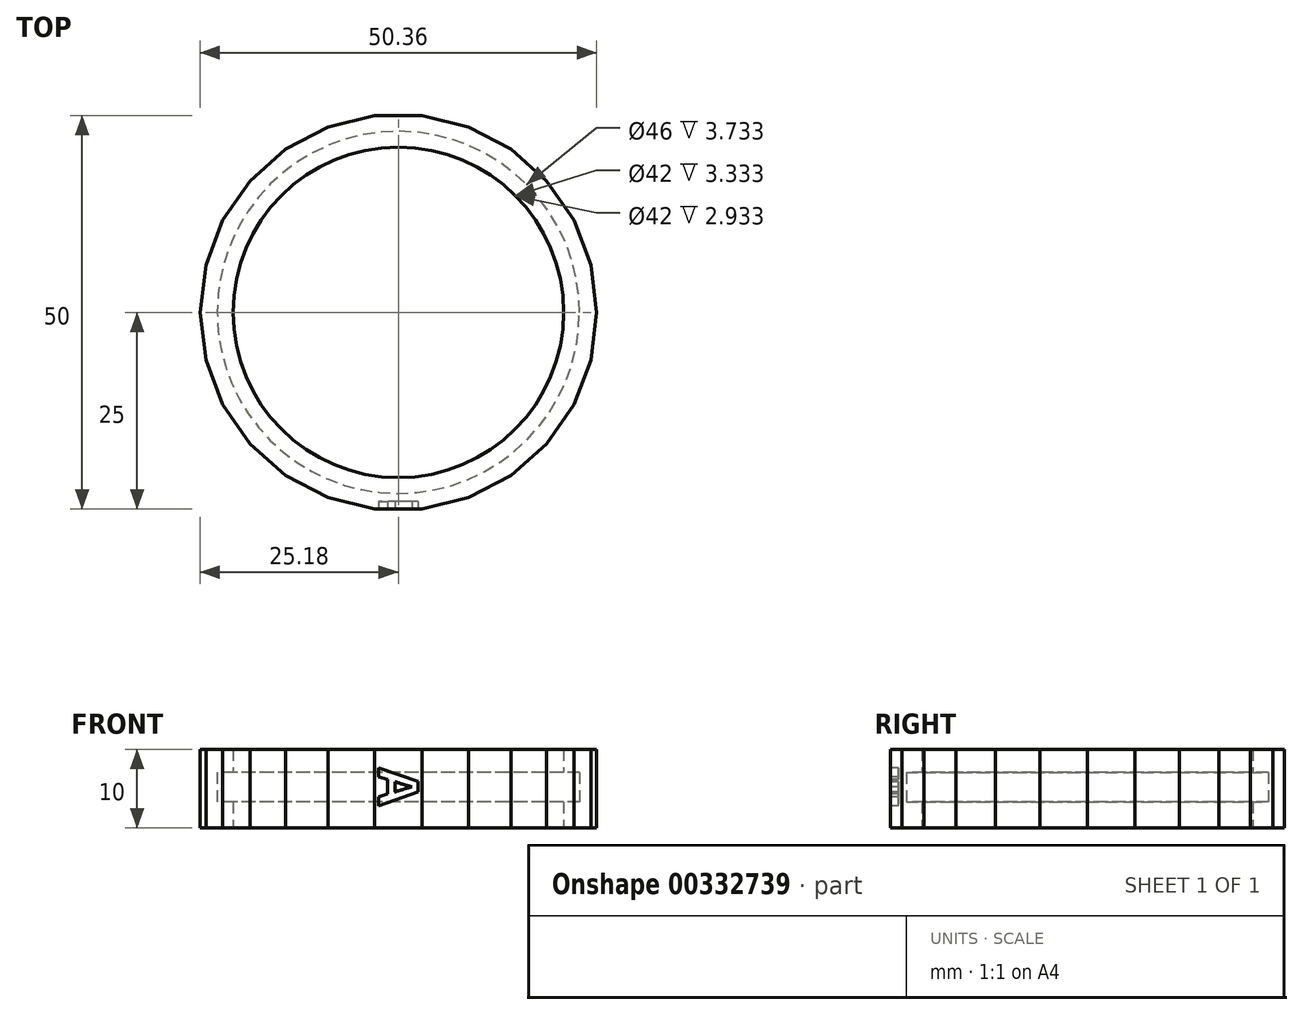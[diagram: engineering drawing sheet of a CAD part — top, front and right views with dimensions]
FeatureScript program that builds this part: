
annotation { "Feature Type Name" : "Feature", "Feature Type Description" : "" }
export const myFeature = defineFeature(function(context is Context, id is Id, definition is map)
    precondition{}
    {
        {
            assignVariable(context, id + "F0", {"name" : "thickness", "anyValue" : 2});
        }
        {
            var Q0;
            Q0=qCreatedBy(makeId("Top.planeOp"),FACE);
            var sketch = newSketch(context, id + "F1", { "sketchPlane" : qUnion([Q0])});
            skCircle(sketch, "E0", {"center": v(0, 0) * mm, "radius": 21 * mm});
            skCircle(sketch, "E1", {"center": v(0, 0) * mm, "radius": 23 * mm});
            skCircle(sketch, "E2.cCircle", {"center": v(0, 0) * mm, "radius": 25 * mm, "construction": true});
            skLineSegment(sketch, "E2.0", {"start": v(-3.04, 25) * mm, "end": v(3.04, 25) * mm});
            skLineSegment(sketch, "E2.1", {"start": v(3.04, 25) * mm, "end": v(8.93, 23.55) * mm});
            skLineSegment(sketch, "E2.2", {"start": v(8.93, 23.55) * mm, "end": v(14.3, 20.73) * mm});
            skLineSegment(sketch, "E2.3", {"start": v(14.3, 20.73) * mm, "end": v(18.85, 16.7) * mm});
            skLineSegment(sketch, "E2.4", {"start": v(18.85, 16.7) * mm, "end": v(22.3, 11.7) * mm});
            skLineSegment(sketch, "E2.5", {"start": v(22.3, 11.7) * mm, "end": v(24.45, 6.03) * mm});
            skLineSegment(sketch, "E2.6", {"start": v(24.45, 6.03) * mm, "end": v(25.18, 0) * mm});
            skLineSegment(sketch, "E2.7", {"start": v(25.18, 0) * mm, "end": v(24.45, -6.03) * mm});
            skLineSegment(sketch, "E2.8", {"start": v(24.45, -6.03) * mm, "end": v(22.3, -11.7) * mm});
            skLineSegment(sketch, "E2.9", {"start": v(22.3, -11.7) * mm, "end": v(18.85, -16.7) * mm});
            skLineSegment(sketch, "E2.10", {"start": v(18.85, -16.7) * mm, "end": v(14.3, -20.73) * mm});
            skLineSegment(sketch, "E2.11", {"start": v(14.3, -20.73) * mm, "end": v(8.93, -23.55) * mm});
            skLineSegment(sketch, "E2.12", {"start": v(8.93, -23.55) * mm, "end": v(3.04, -25) * mm});
            skLineSegment(sketch, "E2.13", {"start": v(3.04, -25) * mm, "end": v(-3.04, -25) * mm});
            skLineSegment(sketch, "E2.14", {"start": v(-3.04, -25) * mm, "end": v(-8.93, -23.55) * mm});
            skLineSegment(sketch, "E2.15", {"start": v(-8.93, -23.55) * mm, "end": v(-14.3, -20.73) * mm});
            skLineSegment(sketch, "E2.16", {"start": v(-14.3, -20.73) * mm, "end": v(-18.85, -16.7) * mm});
            skLineSegment(sketch, "E2.17", {"start": v(-18.85, -16.7) * mm, "end": v(-22.3, -11.7) * mm});
            skLineSegment(sketch, "E2.18", {"start": v(-22.3, -11.7) * mm, "end": v(-24.45, -6.03) * mm});
            skLineSegment(sketch, "E2.19", {"start": v(-24.45, -6.03) * mm, "end": v(-25.18, 0) * mm});
            skLineSegment(sketch, "E2.20", {"start": v(-25.18, 0) * mm, "end": v(-24.45, 6.03) * mm});
            skLineSegment(sketch, "E2.21", {"start": v(-24.45, 6.03) * mm, "end": v(-22.3, 11.7) * mm});
            skLineSegment(sketch, "E2.22", {"start": v(-22.3, 11.7) * mm, "end": v(-18.85, 16.7) * mm});
            skLineSegment(sketch, "E2.23", {"start": v(-18.85, 16.7) * mm, "end": v(-14.3, 20.73) * mm});
            skLineSegment(sketch, "E2.24", {"start": v(-14.3, 20.73) * mm, "end": v(-8.93, 23.55) * mm});
            skLineSegment(sketch, "E2.25", {"start": v(-8.93, 23.55) * mm, "end": v(-3.04, 25) * mm});
            skPoint(sketch, "E2.0.midPoint", {"position": v(0, 25) * mm});
            skSolve(sketch);
        }
        {
            var Q0;
            Q0=qCreatedBy(makeId("Front.planeOp"),FACE);
            var sketch = newSketch(context, id + "F2", { "sketchPlane" : qUnion([Q0])});
            skLineSegment(sketch, "E3", {"start": v(0, 10) * mm, "end": v(0, 0) * mm, "construction": true});
            skPoint(sketch, "E4", {"position": v(0, 10.4) * mm});
            skPoint(sketch, "E5", {"position": v(0, 6.67) * mm});
            skPoint(sketch, "E6", {"position": v(0, 3.33) * mm});
            skPoint(sketch, "E7", {"position": v(0, 3.73) * mm});
            skPoint(sketch, "E8", {"position": v(0, 7.07) * mm});
            skPoint(sketch, "E9", {"position": v(0, 5) * mm});
            skPoint(sketch, "E10", {"position": v(0, 5.4) * mm});
            skSolve(sketch);
        }
        {
            var Q0;
            Q0=makeQuery(id+"F1.imprint","IMPRINT",FACE,{"disambiguationData":[TD([[makeQuery(id+"F1.imprint","IMPRINT",EDGE,{"derivedFrom":sQuery(id+"F1.wireOp",EDGE,"E1")}),-1.0]])]});
            var Q1;
            Q1=sQuery(id+"F2.wireOp",VERTEX,"E3.start");
            extrude(context, id + "F3", {"entities" : qUnion([Q0]), "endBound" : BoundingType.UP_TO_VERTEX, "endBoundEntityVertex" : qUnion([Q1]), "depth" : 25 * mm});
        }
        {
            var Q0;
            Q0=makeQuery(id+"F1.imprint","IMPRINT",FACE,{"disambiguationData":[TD([[makeQuery(id+"F1.imprint","IMPRINT",EDGE,{"derivedFrom":sQuery(id+"F1.wireOp",EDGE,"E0")}),-1.0]])]});
            var Q1;
            Q1=sQuery(id+"F2.wireOp",VERTEX,"E6");
            var Q2;
            Q2=sQuery(id+"F2.wireOp",VERTEX,"E6");
            extrude(context, id + "F4", {"entities" : qUnion([Q0]), "operationType" : NewBodyOperationType.ADD, "endBound" : BoundingType.UP_TO_VERTEX, "endBoundEntityVertex" : qUnion([Q1]), "depth" : 25 * mm});
        }
        {
            var Q0;
            Q0=makeQuery(id+"F1.imprint","IMPRINT",FACE,{"disambiguationData":[TD([[makeQuery(id+"F1.imprint","IMPRINT",EDGE,{"derivedFrom":sQuery(id+"F1.wireOp",EDGE,"E0")}),-1.0]])]});
            var Q1;
            Q1=sQuery(id+"F2.wireOp",VERTEX,"E3.start");
            var Q2;
            Q2=sQuery(id+"F2.wireOp",VERTEX,"E8");
            extrude(context, id + "F5", {"entities" : qUnion([Q0]), "operationType" : NewBodyOperationType.ADD, "endBound" : BoundingType.UP_TO_VERTEX, "endBoundEntityVertex" : qUnion([Q1]), "depth" : 25 * mm, "hasSecondDirection" : true, "secondDirectionBound" : BoundingType.UP_TO_VERTEX, "secondDirectionOppositeDirection" : false, "secondDirectionBoundEntityVertex" : qUnion([Q2]), "secondDirectionDepth" : 25 * mm});
        }
        {
            var Q0;
            Q0=makeQuery(id+"F3.opExtrude","SWEPT_FACE",FACE,{"disambiguationData":[OSD([sQuery(id+"F1.wireOp",EDGE,"E2.13")])]});
            var sketch = newSketch(context, id + "F6", { "sketchPlane" : qUnion([Q0])});
            skText(sketch, "E11", { "text": "A", "fontName": "OpenSans-Bold.ttf"});
            const initialGuessF6  = {"E11": [-0.00254, 0.00766, 0, -1, 0.00507]};
            skSetInitialGuess(sketch, initialGuessF6);
            skSolve(sketch);
        }
        {
            var Q0;
            Q0=makeQuery(id+"F6.imprint","IMPRINT",FACE,{"disambiguationData":[TD([[makeQuery(id+"F6.imprint","IMPRINT",EDGE,{"derivedFrom":sQuery(id+"F6.wireOp",EDGE,"E11.sketch_text.stroke-0")}),-1.0]])]});
            extrude(context, id + "F7", {"entities" : qUnion([Q0]), "operationType" : NewBodyOperationType.REMOVE, "oppositeDirection" : true, "depth" : (getVariable(context, 'thickness') * .49) * mm});
        }
    });
